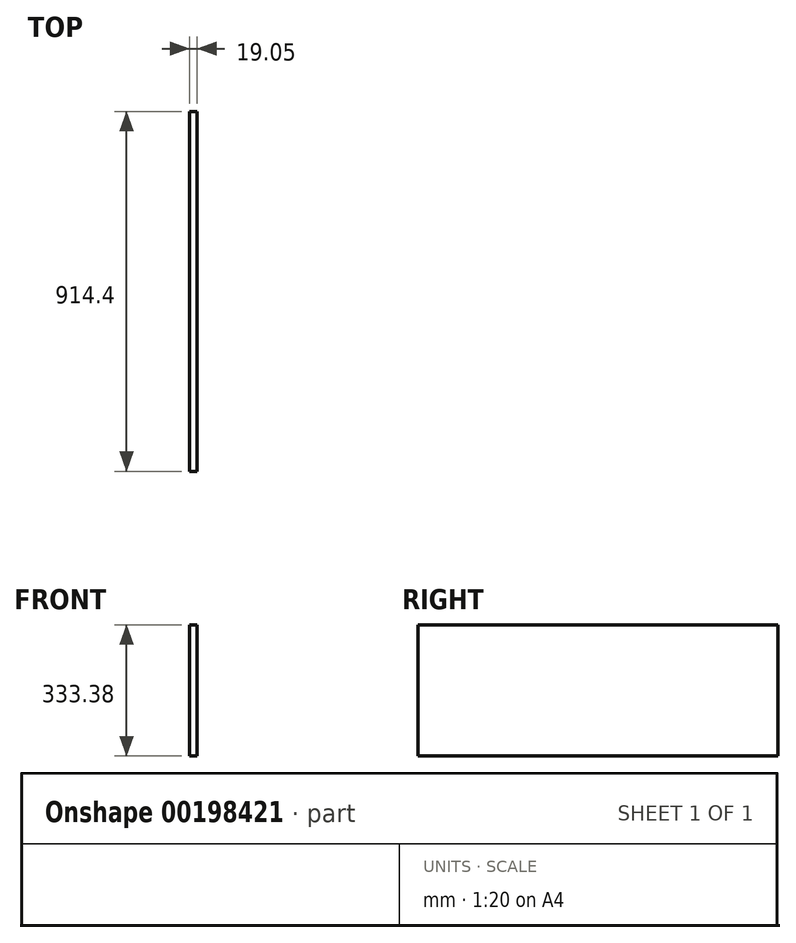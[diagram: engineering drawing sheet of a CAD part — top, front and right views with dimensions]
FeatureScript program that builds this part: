
annotation { "Feature Type Name" : "Feature", "Feature Type Description" : "" }
export const myFeature = defineFeature(function(context is Context, id is Id, definition is map)
    precondition{}
    {
        {
            var Q0;
            Q0=qCreatedBy(makeId("Right.planeOp"),FACE);
            var sketch = newSketch(context, id + "F0", { "sketchPlane" : qUnion([Q0])});
            skLineSegment(sketch, "E0.bottom", {"start": v(0, 0) * mm, "end": v(914.4, 0) * mm});
            skLineSegment(sketch, "E0.top", {"start": v(0, 333.38) * mm, "end": v(914.4, 333.38) * mm});
            skLineSegment(sketch, "E0.left", {"start": v(0, 0) * mm, "end": v(0, 333.38) * mm});
            skLineSegment(sketch, "E0.right", {"start": v(914.4, 0) * mm, "end": v(914.4, 333.38) * mm});
            skSolve(sketch);
        }
        {
            var Q0;
            Q0=makeQuery(id+"F0.imprint","IMPRINT",FACE,{"disambiguationData":[TD([[makeQuery(id+"F0.imprint","IMPRINT",EDGE,{"derivedFrom":sQuery(id+"F0.wireOp",EDGE,"E0.bottom")}),1.0]])]});
            extrude(context, id + "F1", {"entities" : qUnion([Q0]), "depth" : 19.05 * mm});
        }
    });
